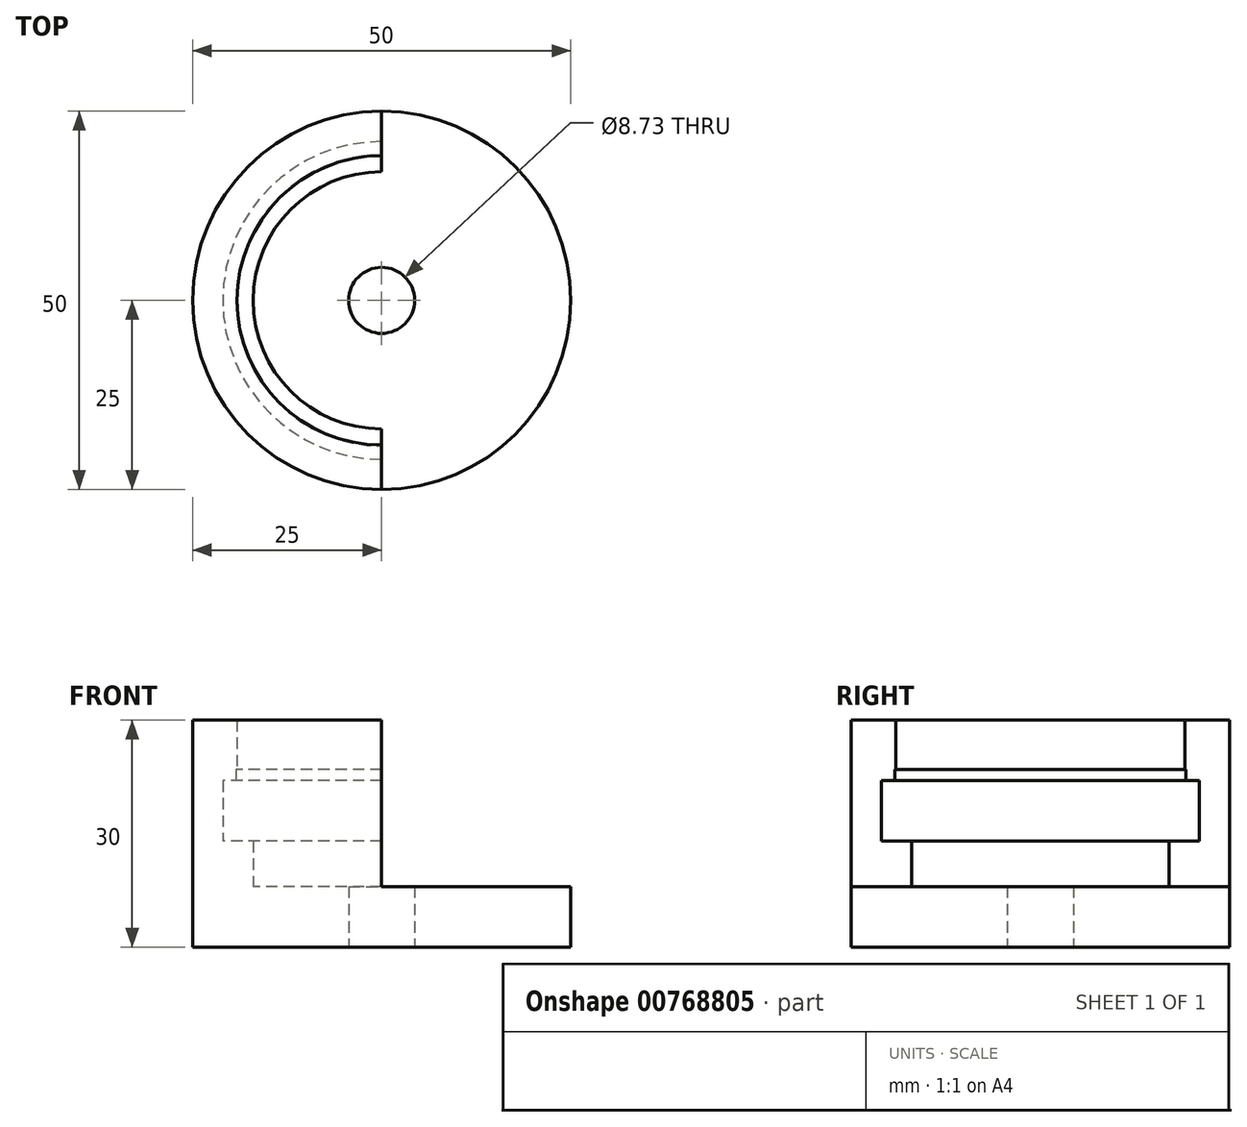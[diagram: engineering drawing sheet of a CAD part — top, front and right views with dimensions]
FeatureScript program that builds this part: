
annotation { "Feature Type Name" : "Feature", "Feature Type Description" : "" }
export const myFeature = defineFeature(function(context is Context, id is Id, definition is map)
    precondition{}
    {
        {
            var Q0;
            Q0=qCreatedBy(makeId("Front.planeOp"),FACE);
            var sketch = newSketch(context, id + "F0", { "sketchPlane" : qUnion([Q0])});
            skLineSegment(sketch, "E0", {"start": v(-4.36, 0) * mm, "end": v(-17, 0) * mm});
            skLineSegment(sketch, "E1", {"start": v(-17, 0) * mm, "end": v(-17, 6) * mm});
            skLineSegment(sketch, "E2", {"start": v(-17, 6) * mm, "end": v(-21, 6) * mm});
            skLineSegment(sketch, "E3", {"start": v(-21, 6) * mm, "end": v(-21, 14) * mm});
            skLineSegment(sketch, "E4", {"start": v(-21, 14) * mm, "end": v(-19.25, 14) * mm});
            skLineSegment(sketch, "E5", {"start": v(-19.25, 14) * mm, "end": v(-19.25, 15.5) * mm});
            skLineSegment(sketch, "E6", {"start": v(-19.25, 15.5) * mm, "end": v(-19.12, 15.5) * mm});
            skLineSegment(sketch, "E7", {"start": v(-19.12, 15.5) * mm, "end": v(-19.12, 22) * mm});
            skLineSegment(sketch, "E8", {"start": v(0, 0) * mm, "end": v(0, 67.04) * mm, "construction": true});
            skLineSegment(sketch, "E9", {"start": v(-4.36, 0) * mm, "end": v(-4.36, -8) * mm});
            skLineSegment(sketch, "E10", {"start": v(-4.36, -8) * mm, "end": v(-25, -8) * mm});
            skLineSegment(sketch, "E11", {"start": v(-25, -8) * mm, "end": v(-25, 22) * mm});
            skLineSegment(sketch, "E12", {"start": v(-25, 22) * mm, "end": v(-19.12, 22) * mm});
            skSolve(sketch);
        }
        {
            var Q0;
            Q0 = qSketchRegion(id + "F0", true);
            var Q1;
            Q1=sQuery(id+"F0.wireOp",EDGE,"E8");
            revolve(context, id + "F1", {"surfaceOperationType" : NewSurfaceOperationType.NEW, "entities" : qUnion([Q0]), "axis" : qUnion([Q1]), "revolveType" : RevolveType.FULL});
        }
        {
            var Q0;
            Q0=qCreatedBy(makeId("Front.planeOp"),FACE);
            var sketch = newSketch(context, id + "F2", { "sketchPlane" : qUnion([Q0])});
            skLineSegment(sketch, "E13", {"start": v(0, 30) * mm, "end": v(0, 0) * mm});
            skLineSegment(sketch, "E14", {"start": v(0, 0) * mm, "end": v(30, 0) * mm});
            skLineSegment(sketch, "E15", {"start": v(0, 30) * mm, "end": v(30, 30) * mm});
            skLineSegment(sketch, "E16", {"start": v(30, 30) * mm, "end": v(30, 0) * mm});
            skSolve(sketch);
        }
        {
            var Q0;
            Q0 = qSketchRegion(id + "F2", true);
            extrude(context, id + "F3", {"entities" : qUnion([Q0]), "operationType" : NewBodyOperationType.REMOVE, "endBound" : BoundingType.THROUGH_ALL, "oppositeDirection" : true, "depth" : 25 * mm, "offsetDistance" : 25 * mm, "hasSecondDirection" : true, "secondDirectionBound" : SecondDirectionBoundingType.THROUGH_ALL, "secondDirectionOppositeDirection" : false, "secondDirectionDepth" : 25 * mm});
        }
    });
